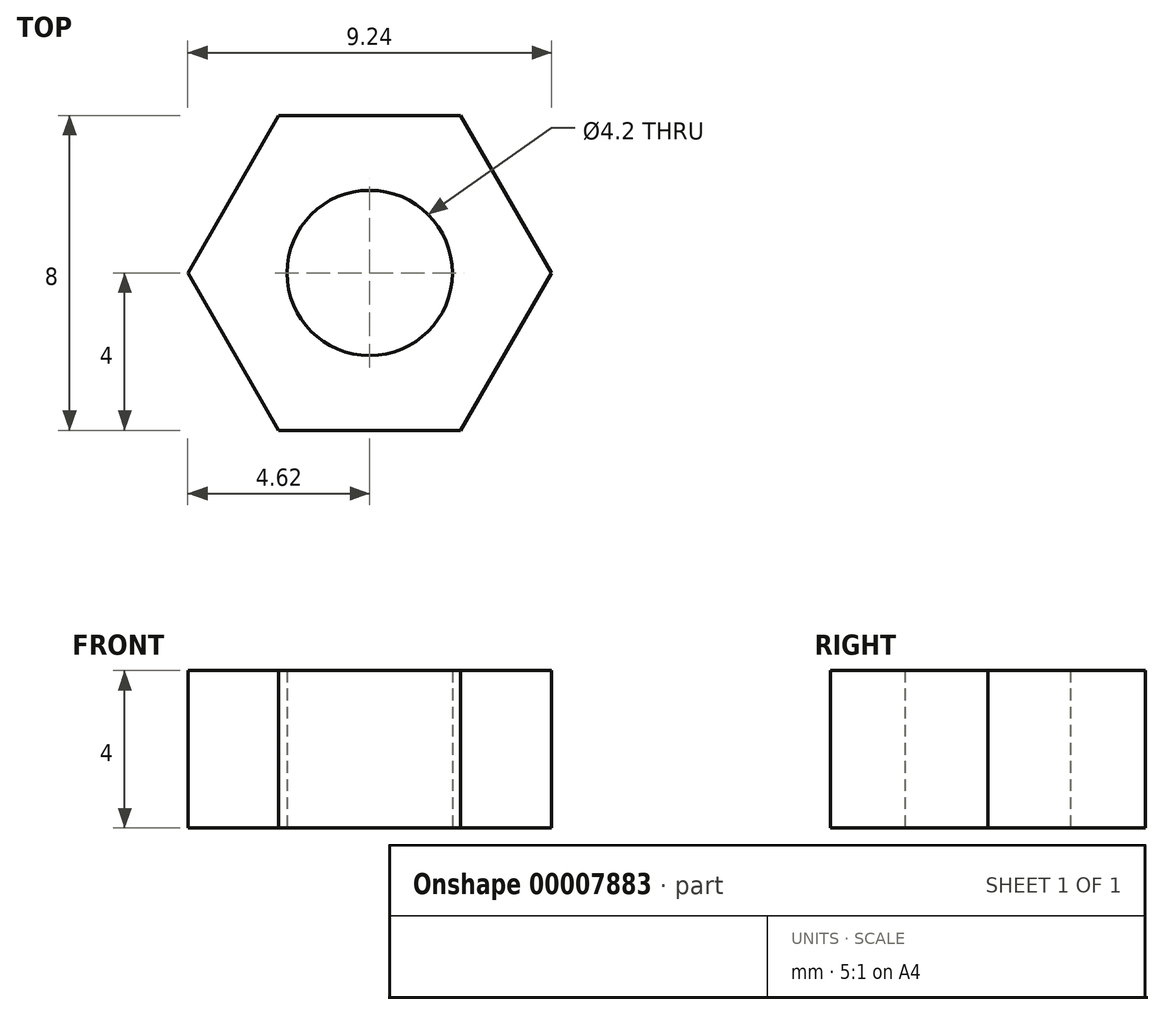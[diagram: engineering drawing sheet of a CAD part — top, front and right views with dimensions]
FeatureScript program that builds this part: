
annotation { "Feature Type Name" : "Feature", "Feature Type Description" : "" }
export const myFeature = defineFeature(function(context is Context, id is Id, definition is map)
    precondition{}
    {
        {
            var Q0;
            Q0=qCreatedBy(makeId("Top.planeOp"),FACE);
            var sketch = newSketch(context, id + "F0", { "sketchPlane" : qUnion([Q0])});
            skCircle(sketch, "E0.cCircle", {"center": v(0, 0) * mm, "radius": 4 * mm, "construction": true});
            skLineSegment(sketch, "E0.0", {"start": v(-2.3, 4) * mm, "end": v(2.3, 4) * mm});
            skLineSegment(sketch, "E0.1", {"start": v(2.3, 4) * mm, "end": v(4.62, 0) * mm});
            skLineSegment(sketch, "E0.2", {"start": v(4.62, 0) * mm, "end": v(2.3, -4) * mm});
            skLineSegment(sketch, "E0.3", {"start": v(2.3, -4) * mm, "end": v(-2.3, -4) * mm});
            skLineSegment(sketch, "E0.4", {"start": v(-2.3, -4) * mm, "end": v(-4.62, 0) * mm});
            skLineSegment(sketch, "E0.5", {"start": v(-4.62, 0) * mm, "end": v(-2.3, 4) * mm});
            skPoint(sketch, "E0.0.midPoint", {"position": v(0, 4) * mm});
            skSolve(sketch);
        }
        {
            var Q0;
            Q0=makeQuery(id+"F0.imprint","IMPRINT",FACE,{"disambiguationData":[TD([[makeQuery(id+"F0.imprint","IMPRINT",EDGE,{"derivedFrom":sQuery(id+"F0.wireOp",EDGE,"E0.0")}),-1.0]])]});
            extrude(context, id + "F1", {"entities" : qUnion([Q0]), "depth" : 4 * mm});
        }
        {
            var Q0;
            Q0=qCreatedBy(makeId("Top.planeOp"),FACE);
            var sketch = newSketch(context, id + "F2", { "sketchPlane" : qUnion([Q0])});
            skCircle(sketch, "E1", {"center": v(0, 0) * mm, "radius": 2.1 * mm});
            skSolve(sketch);
        }
        {
            var Q0;
            Q0=qSketchRegion(id+"F2",true);
            extrude(context, id + "F3", {"entities" : qUnion([Q0]), "operationType" : NewBodyOperationType.REMOVE, "endBound" : BoundingType.UP_TO_NEXT, "depth" : 60 * mm});
        }
    });
